# Revit family: Chariot Booth Windows - ES Width
name_source: partatom
category: Furniture
units: mm (PartAtom-declared; Revit-internal decimal feet)

## family parameters
Always vertical = Yes
Cut with Voids When Loaded = No
OmniClass Number = 23.40.20.00
OmniClass Title = General Furniture and Specialties
Room Calculation Point = No
Shared = No
Work Plane-Based = No

## types (6) — shared parameters
Default Elevation = 0' - 0"

## per-type parameters (varying)
| type | ES Seat Count | HS Seat Count | Model | UK Primary Seat Count | UK Secondary Seat Count | Width | Window 12" | Window 6" | Window Height | Window Width |
| BOOTH20-42FB-6W | 4 | 4 | BOOTH20-42FB | 4 | 4 | 3' - 6" | No | Yes | 0' - 5 11/16" | 2' - 9 3/8" |
| BOOTH20-60FB-6W | 6 | 6 | BOOTH20-60FB | 6 | 6 | 5' - 0" | No | Yes | 0' - 5 11/16" | 3' - 9 3/8" |
| BOOTH20-48FB-6W | 4 | 4 | BOOTH20-48FB | 4 | 4 | 4' - 0" | No | Yes | 0' - 5 11/16" | 3' - 1 3/8" |
| BOOTH20-42FB-12W | 4 | 4 | BOOTH20-42FB | 4 | 4 | 3' - 6" | Yes | No | 0' - 11 11/16" | 2' - 9 3/8" |
| BOOTH20-48FB-12W | 4 | 4 | BOOTH20-48FB | 4 | 4 | 4' - 0" | Yes | No | 0' - 11 11/16" | 3' - 1 3/8" |
| BOOTH20-60FB-12W | 6 | 6 | BOOTH20-60FB | 6 | 6 | 5' - 0" | Yes | No | 0' - 11 11/16" | 3' - 9 3/8" |

## geometry (parser evidence)
native form markers: Sweep x7
no freeform markers — native parametric forms only
